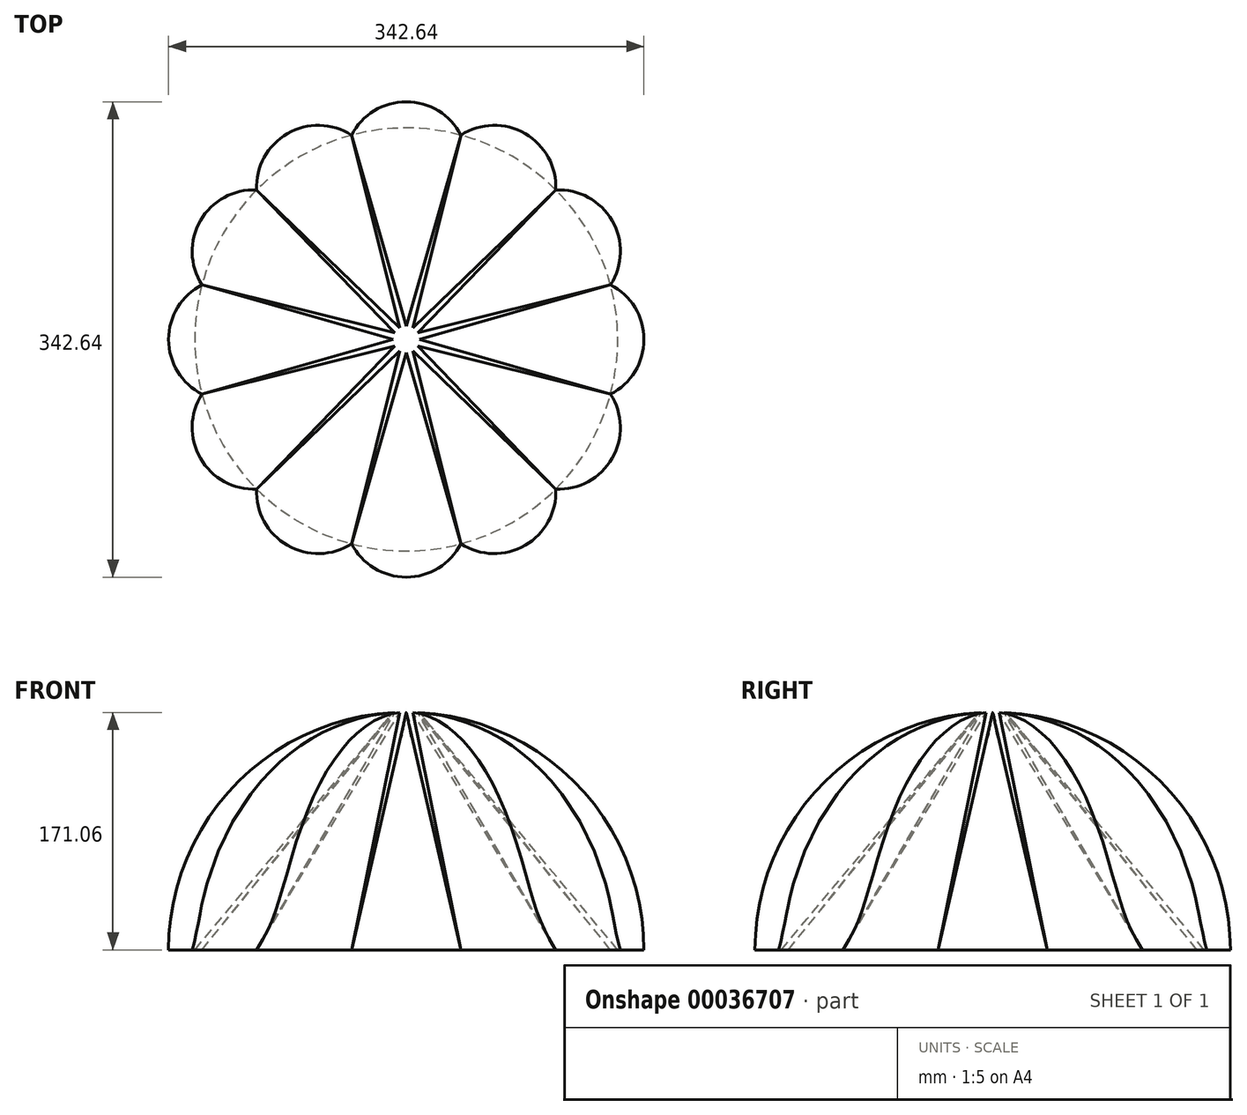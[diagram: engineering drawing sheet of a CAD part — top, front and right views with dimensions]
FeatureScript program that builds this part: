
annotation { "Feature Type Name" : "Feature", "Feature Type Description" : "" }
export const myFeature = defineFeature(function(context is Context, id is Id, definition is map)
    precondition{}
    {
        {
            var Q0;
            Q0=qCreatedBy(makeId("Top.planeOp"),FACE);
            var sketch = newSketch(context, id + "F0", { "sketchPlane" : qUnion([Q0])});
            skCircle(sketch, "E0", {"center": v(0, 0) * mm, "radius": 152.4 * mm});
            skLineSegment(sketch, "E1", {"start": v(0, 0) * mm, "end": v(0, 254) * mm, "construction": true});
            skLineSegment(sketch, "E2", {"start": v(0, 0) * mm, "end": v(0, -254) * mm, "construction": true});
            skArc(sketch, "E3", {"start": v(-39.44, -147.2) * mm, "mid": v(0, -171.32) * mm, "end": v(39.44, -147.2) * mm});
            skCircle(sketch, "E4", {"center": v(0, 0) * mm, "radius": 127 * mm});
            skLineSegment(sketch, "E5", {"start": v(-65.74, -245.35) * mm, "end": v(0, 0) * mm, "construction": true});
            skLineSegment(sketch, "E6", {"start": v(65.74, -245.35) * mm, "end": v(0, 0) * mm, "construction": true});
            skLineSegment(sketch, "E7", {"start": v(-39.44, -147.2) * mm, "end": v(-32.87, -122.67) * mm});
            skLineSegment(sketch, "E8", {"start": v(39.44, -147.2) * mm, "end": v(32.87, -122.67) * mm});
            skPoint(sketch, "E9", {"position": v(0, 152.4) * mm});
            skPoint(sketch, "E10", {"position": v(0, 127) * mm});
            skLineSegment(sketch, "E11", {"start": v(0, 0) * mm, "end": v(254, 0) * mm, "construction": true});
            skLineSegment(sketch, "E12", {"start": v(0, 0) * mm, "end": v(-254, 0) * mm, "construction": true});
            skPoint(sketch, "E13", {"position": v(0, -152.4) * mm});
            skPoint(sketch, "E14", {"position": v(0, -171.32) * mm});
            skSolve(sketch);
        }
        {
            var Q0;
            Q0=qCreatedBy(makeId("Right.planeOp"),FACE);
            var sketch = newSketch(context, id + "F1", { "sketchPlane" : qUnion([Q0])});
            skLineSegment(sketch, "E15", {"start": v(0, 0) * mm, "end": v(0, 171.32) * mm, "construction": true});
            skPoint(sketch, "E16.0", {"position": v(-127, 0) * mm});
            skPoint(sketch, "E17.1", {"position": v(-152.4, 0) * mm});
            skLineSegment(sketch, "E18.2", {"start": v(0, 0) * mm, "end": v(-254, 0) * mm, "construction": true});
            skPoint(sketch, "E19.0", {"position": v(-171.32, 0) * mm});
            skLineSegment(sketch, "E20", {"start": v(0, 0) * mm, "end": v(-9.5, 171.06) * mm, "construction": true});
            skArc(sketch, "E21", {"start": v(-7.04, 126.8) * mm, "mid": v(-92.26, 87.28) * mm, "end": v(-127, 0) * mm});
            skArc(sketch, "E22", {"start": v(-8.45, 152.17) * mm, "mid": v(-110.7, 104.73) * mm, "end": v(-152.4, 0) * mm});
            skArc(sketch, "E23", {"start": v(-9.5, 171.06) * mm, "mid": v(-124.45, 117.74) * mm, "end": v(-171.32, 0) * mm});
            skSolve(sketch);
        }
        {
            var Q0;
            {var subQ0=sQuery(id+"F0.wireOp",EDGE,"E3");Q0=makeQuery(id+"F0.imprint","IMPRINT",FACE,{"disambiguationData":[TD([[makeQuery(id+"F0.imprint","IMPRINT",EDGE,{"derivedFrom":subQ0}),1.0]])]});}
            var Q1;
            Q1=sQuery(id+"F1.wireOp",VERTEX,"E23.start");
            var Q2;
            Q2=sQuery(id+"F1.wireOp",EDGE,"E23");
            loft(context, id + "F2", {"addGuides" : true, "sheetProfilesArray" : [{ "sheetProfileEntities" : qUnion([Q0]) }, { "sheetProfileEntities" : qUnion([Q1]) }], "guidesArray" : [{ "guideEntities" : qUnion([Q2]), "guideDerivativeType" : LoftGuideDerivativeType.DEFAULT, "guideDerivativeMagnitude" : 1 }]});
        }
        {
            var Q0;
            {var subQ0=sQuery(id+"F0.wireOp",EDGE,"E3");Q0=makeQuery(id+"F2.opLoft","SWEPT_BODY",BODY,{"disambiguationData":[OSD([makeQuery(id+"F0.imprint","IMPRINT",FACE,{"disambiguationData":[TD([[makeQuery(id+"F0.imprint","IMPRINT",EDGE,{"derivedFrom":subQ0}),1.0]])]}),sQuery(id+"F1.wireOp",VERTEX,"E23.start"),sQuery(id+"F1.wireOp",EDGE,"E23")])]});}
            var Q1;
            Q1=sQuery(id+"F1.wireOp",EDGE,"E15");
            circularPattern(context, id + "F3", {"operationType" : NewBodyOperationType.ADD, "entities" : qUnion([Q0]), "axis" : qUnion([Q1]), "angle" : 30 * degree, "instanceCount" : 13});
        }
    });
